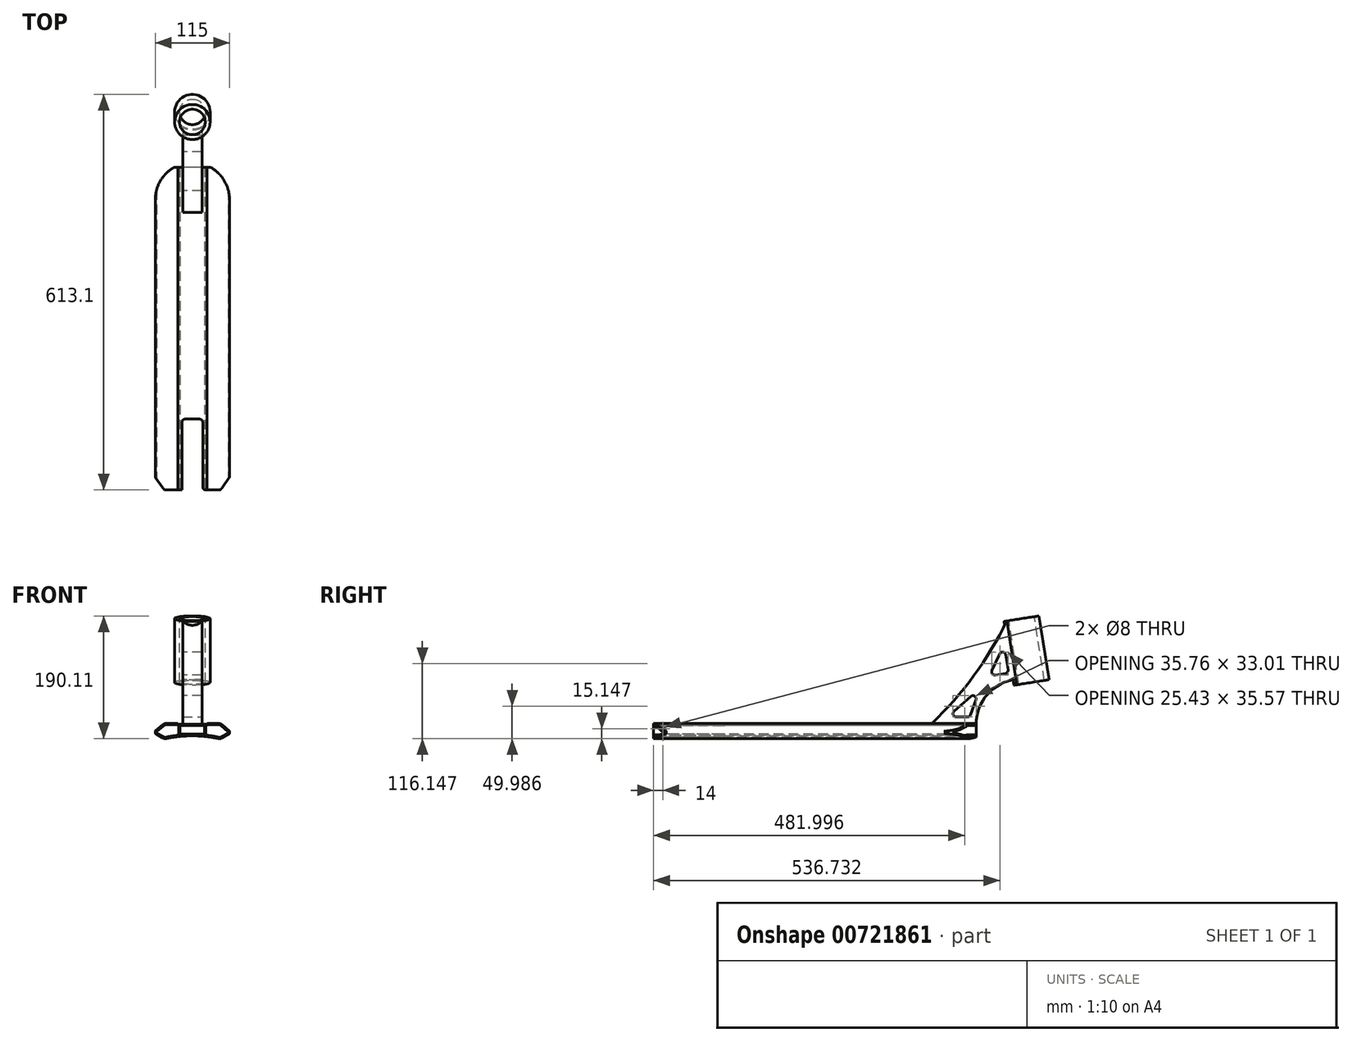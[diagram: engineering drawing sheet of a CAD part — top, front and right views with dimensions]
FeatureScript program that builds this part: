
annotation { "Feature Type Name" : "Feature", "Feature Type Description" : "" }
export const myFeature = defineFeature(function(context is Context, id is Id, definition is map)
    precondition{}
    {
        {
            var Q0;
            Q0=qCreatedBy(makeId("Front.planeOp"),FACE);
            var sketch = newSketch(context, id + "F0", { "sketchPlane" : qUnion([Q0])});
            skLineSegment(sketch, "E0", {"start": v(57.5, 12.15) * mm, "end": v(57.5, 8.15) * mm});
            skLineSegment(sketch, "E1", {"start": v(57.5, 8.15) * mm, "end": v(43.38, 0) * mm});
            skLineSegment(sketch, "E2", {"start": v(0, 0) * mm, "end": v(0, 30.07) * mm, "construction": true});
            skLineSegment(sketch, "E3.MirrorCS", {"start": v(-57.5, 8.15) * mm, "end": v(-43.38, 0) * mm});
            skLineSegment(sketch, "E4.MirrorCS", {"start": v(-57.5, 12.15) * mm, "end": v(-57.5, 8.15) * mm});
            skLineSegment(sketch, "E5", {"start": v(22.5, 24) * mm, "end": v(43.38, 24) * mm});
            skLineSegment(sketch, "E6", {"start": v(43.38, 24) * mm, "end": v(57.5, 12.15) * mm});
            skLineSegment(sketch, "E7.MirrorCS", {"start": v(-22.5, 24) * mm, "end": v(-43.38, 24) * mm});
            skLineSegment(sketch, "E8.MirrorCS", {"start": v(-43.38, 24) * mm, "end": v(-57.5, 12.15) * mm});
            skLineSegment(sketch, "E9", {"start": v(-22.5, 24) * mm, "end": v(-22.5, 22.7) * mm});
            skLineSegment(sketch, "E10", {"start": v(-22.5, 22.7) * mm, "end": v(0, 22.7) * mm});
            skLineSegment(sketch, "E11.MirrorCS", {"start": v(22.5, 24) * mm, "end": v(22.5, 22.7) * mm});
            skLineSegment(sketch, "E12.MirrorCS", {"start": v(22.5, 22.7) * mm, "end": v(0, 22.7) * mm});
            skLineSegment(sketch, "E13", {"start": v(-43.38, 24) * mm, "end": v(-71.32, 24) * mm, "construction": true});
            skLineSegment(sketch, "E14", {"start": v(-57.5, 8.15) * mm, "end": v(-57.5, -4.9) * mm, "construction": true});
            skArc(sketch, "E15", {"start": v(43.38, 0) * mm, "mid": v(0, 4.76) * mm, "end": v(-43.38, 0) * mm});
            skSolve(sketch);
        }
        {
            var Q0;
            Q0=makeQuery(id+"F0.imprint","IMPRINT",FACE,{"disambiguationData":[TD([[makeQuery(id+"F0.imprint","IMPRINT",EDGE,{"derivedFrom":sQuery(id+"F0.wireOp",EDGE,"E0")}),-1.0]])]});
            extrude(context, id + "F1", {"entities" : qUnion([Q0]), "endBound" : BoundingType.SYMMETRIC, "depth" : 500 * mm, "offsetDistance" : 25 * mm});
        }
        {
            var Q0;
            Q0=makeQuery(id+"F1.opExtrude","CAP_FACE",FACE,{"disambiguationData":[OSD([sQuery(id+"F0.wireOp",EDGE,"E0"),sQuery(id+"F0.wireOp",EDGE,"E1"),sQuery(id+"F0.wireOp",EDGE,"E3.MirrorCS"),sQuery(id+"F0.wireOp",EDGE,"E4.MirrorCS"),sQuery(id+"F0.wireOp",EDGE,"E5"),sQuery(id+"F0.wireOp",EDGE,"E6"),sQuery(id+"F0.wireOp",EDGE,"E7.MirrorCS"),sQuery(id+"F0.wireOp",EDGE,"E8.MirrorCS"),sQuery(id+"F0.wireOp",EDGE,"E9"),sQuery(id+"F0.wireOp",EDGE,"E10"),sQuery(id+"F0.wireOp",EDGE,"E11.MirrorCS"),sQuery(id+"F0.wireOp",EDGE,"E12.MirrorCS"),sQuery(id+"F0.wireOp",EDGE,"E15")])],"isStart":false});
            var sketch = newSketch(context, id + "F2", { "sketchPlane" : qUnion([Q0])});
            skLineSegment(sketch, "E16.bottom", {"start": v(19, 7.7) * mm, "end": v(-19, 7.7) * mm});
            skLineSegment(sketch, "E16.top", {"start": v(19, 20.7) * mm, "end": v(-19, 20.7) * mm});
            skLineSegment(sketch, "E16.left", {"start": v(19, 7.7) * mm, "end": v(19, 20.7) * mm});
            skLineSegment(sketch, "E16.right", {"start": v(-19, 7.7) * mm, "end": v(-19, 20.7) * mm});
            skPoint(sketch, "E16.middle", {"position": v(0, 14.2) * mm});
            skSolve(sketch);
        }
        {
            var Q0;
            Q0 = qSketchRegion(id + "F2", true);
            extrude(context, id + "F3", {"entities" : qUnion([Q0]), "operationType" : NewBodyOperationType.REMOVE, "endBound" : BoundingType.SYMMETRIC, "oppositeDirection" : true, "depth" : 1056 * mm, "offsetDistance" : 25 * mm});
        }
        {
            var Q0;
            Q0=makeQuery(id+"F1.opExtrude","SWEPT_EDGE",EDGE,{"disambiguationData":[OSD([sQuery(id+"F0.wireOp",EDGE,"E7.MirrorCS"),sQuery(id+"F0.wireOp",EDGE,"E8.MirrorCS")])]});
            var Q1;
            Q1=makeQuery(id+"F1.opExtrude","SWEPT_EDGE",EDGE,{"disambiguationData":[OSD([sQuery(id+"F0.wireOp",EDGE,"E3.MirrorCS"),sQuery(id+"F0.wireOp",EDGE,"E15")])]});
            var Q2;
            Q2=makeQuery(id+"F1.opExtrude","SWEPT_EDGE",EDGE,{"disambiguationData":[OSD([sQuery(id+"F0.wireOp",EDGE,"E5"),sQuery(id+"F0.wireOp",EDGE,"E6")])]});
            var Q3;
            Q3=makeQuery(id+"F1.opExtrude","SWEPT_EDGE",EDGE,{"disambiguationData":[OSD([sQuery(id+"F0.wireOp",EDGE,"E1"),sQuery(id+"F0.wireOp",EDGE,"E15")])]});
            fillet(context, id + "F4", {"entities" : qUnion([Q0, Q1, Q2, Q3]), "radius" : 9 * mm, "tangentPropagation" : true, "allowEdgeOverflow" : false});
        }
        {
            var Q0;
            Q0=makeQuery(id+"F1.opExtrude","SWEPT_EDGE",EDGE,{"disambiguationData":[OSD([sQuery(id+"F0.wireOp",EDGE,"E4.MirrorCS"),sQuery(id+"F0.wireOp",EDGE,"E8.MirrorCS")])]});
            var Q1;
            Q1=makeQuery(id+"F1.opExtrude","SWEPT_EDGE",EDGE,{"disambiguationData":[OSD([sQuery(id+"F0.wireOp",EDGE,"E3.MirrorCS"),sQuery(id+"F0.wireOp",EDGE,"E4.MirrorCS")])]});
            var Q2;
            Q2=makeQuery(id+"F1.opExtrude","SWEPT_EDGE",EDGE,{"disambiguationData":[OSD([sQuery(id+"F0.wireOp",EDGE,"E0"),sQuery(id+"F0.wireOp",EDGE,"E6")])]});
            var Q3;
            Q3=makeQuery(id+"F1.opExtrude","SWEPT_EDGE",EDGE,{"disambiguationData":[OSD([sQuery(id+"F0.wireOp",EDGE,"E0"),sQuery(id+"F0.wireOp",EDGE,"E1")])]});
            fillet(context, id + "F5", {"entities" : qUnion([Q0, Q1, Q2, Q3]), "radius" : 1 * mm, "tangentPropagation" : true, "allowEdgeOverflow" : false});
        }
        {
            var Q0;
            Q0=makeQuery(id+"F1.opExtrude","SWEPT_EDGE",EDGE,{"disambiguationData":[OSD([sQuery(id+"F0.wireOp",EDGE,"E7.MirrorCS"),sQuery(id+"F0.wireOp",EDGE,"E9")])]});
            var Q1;
            Q1=makeQuery(id+"F1.opExtrude","SWEPT_EDGE",EDGE,{"disambiguationData":[OSD([sQuery(id+"F0.wireOp",EDGE,"E5"),sQuery(id+"F0.wireOp",EDGE,"E11.MirrorCS")])]});
            fillet(context, id + "F6", {"entities" : qUnion([Q0, Q1]), "radius" : 2 * mm, "tangentPropagation" : true, "allowEdgeOverflow" : false});
        }
        {
            var Q0;
            Q0=makeQuery(id+"F1.opExtrude","CAP_FACE",FACE,{"disambiguationData":[OSD([sQuery(id+"F0.wireOp",EDGE,"E0"),sQuery(id+"F0.wireOp",EDGE,"E1"),sQuery(id+"F0.wireOp",EDGE,"E3.MirrorCS"),sQuery(id+"F0.wireOp",EDGE,"E4.MirrorCS"),sQuery(id+"F0.wireOp",EDGE,"E5"),sQuery(id+"F0.wireOp",EDGE,"E6"),sQuery(id+"F0.wireOp",EDGE,"E7.MirrorCS"),sQuery(id+"F0.wireOp",EDGE,"E8.MirrorCS"),sQuery(id+"F0.wireOp",EDGE,"E9"),sQuery(id+"F0.wireOp",EDGE,"E10"),sQuery(id+"F0.wireOp",EDGE,"E11.MirrorCS"),sQuery(id+"F0.wireOp",EDGE,"E12.MirrorCS"),sQuery(id+"F0.wireOp",EDGE,"E15")])],"isStart":false});
            var sketch = newSketch(context, id + "F7", { "sketchPlane" : qUnion([Q0])});
            skArc(sketch, "E17.0", {"start": v(40.47, 2.67) * mm, "mid": v(0, 6.76) * mm, "end": v(-40.47, 2.67) * mm});
            skArc(sketch, "E17.1", {"start": v(-45.38, 3.46) * mm, "mid": v(-43, 2.61) * mm, "end": v(-40.47, 2.67) * mm});
            skLineSegment(sketch, "E17.2", {"start": v(-55, 9.02) * mm, "end": v(-45.38, 3.46) * mm});
            skLineSegment(sketch, "E17.3", {"start": v(-55.5, 10.75) * mm, "end": v(-55.5, 9.88) * mm});
            skLineSegment(sketch, "E17.4", {"start": v(-24.37, 22) * mm, "end": v(-24.37, 22) * mm});
            skLineSegment(sketch, "E17.5", {"start": v(-24.37, 22) * mm, "end": v(-40.1, 22) * mm});
            skArc(sketch, "E17.6", {"start": v(-40.1, 22) * mm, "mid": v(-42.5, 21.58) * mm, "end": v(-44.6, 20.36) * mm});
            skLineSegment(sketch, "E17.7", {"start": v(-44.6, 20.36) * mm, "end": v(-55.14, 11.52) * mm});
            skLineSegment(sketch, "E18.0", {"start": v(-21, 7.7) * mm, "end": v(-21, 20.7) * mm});
            skLineSegment(sketch, "E19.0", {"start": v(19, 20.7) * mm, "end": v(-19, 20.7) * mm});
            skLineSegment(sketch, "E20.0", {"start": v(-22.5, 20.7) * mm, "end": v(22.5, 20.7) * mm});
            skArc(sketch, "E21", {"start": v(-22.5, 20.7) * mm, "mid": v(-23.23, 21.64) * mm, "end": v(-24.37, 22) * mm});
            skLineSegment(sketch, "E22", {"start": v(-21, 7.7) * mm, "end": v(-21, 5.67) * mm});
            skLineSegment(sketch, "E23", {"start": v(0, 0) * mm, "end": v(0, 29.53) * mm});
            skPoint(sketch, "E23.endSnap0", {"position": v(0, 22.7) * mm});
            skLineSegment(sketch, "E24.MirrorCS", {"start": v(21, 7.7) * mm, "end": v(21, 5.67) * mm});
            skLineSegment(sketch, "E25.MirrorCS", {"start": v(21, 7.7) * mm, "end": v(21, 20.7) * mm});
            skLineSegment(sketch, "E26.MirrorCS", {"start": v(22.5, 20.7) * mm, "end": v(-22.5, 20.7) * mm});
            skArc(sketch, "E27.MirrorCS", {"start": v(22.5, 20.7) * mm, "mid": v(23.23, 21.64) * mm, "end": v(24.37, 22) * mm});
            skLineSegment(sketch, "E28.MirrorCS", {"start": v(24.37, 22) * mm, "end": v(40.1, 22) * mm});
            skArc(sketch, "E29.MirrorCS", {"start": v(40.1, 22) * mm, "mid": v(42.5, 21.58) * mm, "end": v(44.6, 20.36) * mm});
            skLineSegment(sketch, "E30.MirrorCS", {"start": v(44.6, 20.36) * mm, "end": v(55.14, 11.52) * mm});
            skLineSegment(sketch, "E31.MirrorCS", {"start": v(55, 9.02) * mm, "end": v(45.38, 3.46) * mm});
            skArc(sketch, "E32.MirrorCS", {"start": v(45.38, 3.46) * mm, "mid": v(43, 2.61) * mm, "end": v(40.47, 2.67) * mm});
            skLineSegment(sketch, "E33.MirrorCS", {"start": v(55.5, 10.75) * mm, "end": v(55.5, 9.88) * mm});
            skPoint(sketch, "E34.visualSharp", {"position": v(-55.5, 11.22) * mm});
            skArc(sketch, "E34.filletArc", {"start": v(-55.14, 11.52) * mm, "mid": v(-55.4, 11.18) * mm, "end": v(-55.5, 10.75) * mm});
            skPoint(sketch, "E35.visualSharp", {"position": v(-55.5, 9.3) * mm});
            skArc(sketch, "E35.filletArc", {"start": v(-55.5, 9.88) * mm, "mid": v(-55.37, 9.38) * mm, "end": v(-55, 9.02) * mm});
            skPoint(sketch, "E36.visualSharp", {"position": v(55.5, 11.22) * mm});
            skArc(sketch, "E36.filletArc", {"start": v(55.5, 10.75) * mm, "mid": v(55.4, 11.18) * mm, "end": v(55.14, 11.52) * mm});
            skPoint(sketch, "E37.visualSharp", {"position": v(55.5, 9.3) * mm});
            skArc(sketch, "E37.filletArc", {"start": v(55, 9.02) * mm, "mid": v(55.37, 9.38) * mm, "end": v(55.5, 9.88) * mm});
            skSolve(sketch);
        }
        {
            var Q0;
            {var subQ3=sQuery(id+"F7.wireOp",EDGE,"E17.1");Q0=makeQuery(id+"F7.imprint","IMPRINT",FACE,{"disambiguationData":[TD([[makeQuery(id+"F7.imprint","IMPRINT",EDGE,{"derivedFrom":subQ3}),1.0]])]});}
            var Q1;
            {var subQ3=sQuery(id+"F7.wireOp",EDGE,"E24.MirrorCS");Q1=makeQuery(id+"F7.imprint","IMPRINT",FACE,{"disambiguationData":[TD([[makeQuery(id+"F7.imprint","IMPRINT",EDGE,{"derivedFrom":subQ3}),1.0]])]});}
            extrude(context, id + "F8", {"entities" : qUnion([Q0, Q1]), "operationType" : NewBodyOperationType.REMOVE, "endBound" : BoundingType.THROUGH_ALL, "oppositeDirection" : true, "depth" : 25 * mm, "offsetDistance" : 25 * mm});
        }
        {
            var Q0;
            Q0=qCreatedBy(makeId("Top.planeOp"),FACE);
            var sketch = newSketch(context, id + "F9", { "sketchPlane" : qUnion([Q0])});
            skArc(sketch, "E38", {"start": v(57.5, 200) * mm, "mid": v(0, 257.5) * mm, "end": v(-57.5, 200) * mm});
            skLineSegment(sketch, "E39", {"start": v(-57.5, 200) * mm, "end": v(-57.5, 280) * mm});
            skLineSegment(sketch, "E40", {"start": v(-57.5, 280) * mm, "end": v(57.5, 280) * mm});
            skLineSegment(sketch, "E41", {"start": v(57.5, 200) * mm, "end": v(57.5, 280) * mm});
            skSolve(sketch);
        }
        {
            var Q0;
            Q0 = qSketchRegion(id + "F9", true);
            extrude(context, id + "F10", {"entities" : qUnion([Q0]), "operationType" : NewBodyOperationType.REMOVE, "endBound" : BoundingType.THROUGH_ALL, "oppositeDirection" : true, "depth" : 25 * mm, "offsetDistance" : 25 * mm, "hasSecondDirection" : true, "secondDirectionBound" : SecondDirectionBoundingType.THROUGH_ALL, "secondDirectionOppositeDirection" : false, "secondDirectionDepth" : 25 * mm});
        }
        {
            var Q0;
            Q0=qCreatedBy(makeId("Top.planeOp"),FACE);
            var sketch = newSketch(context, id + "F11", { "sketchPlane" : qUnion([Q0])});
            skLineSegment(sketch, "E42", {"start": v(-68, -346) * mm, "end": v(-68, -216) * mm});
            skLineSegment(sketch, "E43", {"start": v(-68, -216) * mm, "end": v(-43.3, -250) * mm});
            skLineSegment(sketch, "E44", {"start": v(-43.3, -250) * mm, "end": v(-16, -250) * mm});
            skLineSegment(sketch, "E45", {"start": v(-16, -250) * mm, "end": v(-16, -140) * mm});
            skLineSegment(sketch, "E46", {"start": v(-16, -140) * mm, "end": v(16, -140) * mm});
            skLineSegment(sketch, "E47", {"start": v(16, -140) * mm, "end": v(16, -250) * mm});
            skLineSegment(sketch, "E48", {"start": v(16, -250) * mm, "end": v(43.3, -250) * mm});
            skLineSegment(sketch, "E49", {"start": v(43.3, -250) * mm, "end": v(68, -216) * mm});
            skLineSegment(sketch, "E50", {"start": v(68, -216) * mm, "end": v(68, -346) * mm});
            skLineSegment(sketch, "E51", {"start": v(68, -346) * mm, "end": v(-68, -346) * mm});
            skLineSegment(sketch, "E52", {"start": v(-68, -346) * mm, "end": v(-68, -346) * mm});
            skSolve(sketch);
        }
        {
            var Q0;
            Q0 = qSketchRegion(id + "F11", true);
            extrude(context, id + "F12", {"entities" : qUnion([Q0]), "operationType" : NewBodyOperationType.REMOVE, "endBound" : BoundingType.THROUGH_ALL, "oppositeDirection" : true, "depth" : 25 * mm, "offsetDistance" : 25 * mm, "hasSecondDirection" : true, "secondDirectionBound" : SecondDirectionBoundingType.THROUGH_ALL, "secondDirectionOppositeDirection" : false, "secondDirectionDepth" : 25 * mm});
        }
        {
            var Q0;
            {var subQ0=sQuery(id+"F11.wireOp",EDGE,"E46");var subQ1=sQuery(id+"F11.wireOp",EDGE,"E45");Q0=makeQuery(id+"F12.boolean.opBoolean","COPY",EDGE,{"disambiguationData":[TD([makeQuery(id+"F3.boolean.opBoolean","COPY",FACE,{"derivedFrom":makeQuery(id+"F3.opExtrude","SWEPT_FACE",FACE,{"disambiguationData":[OSD([sQuery(id+"F2.wireOp",EDGE,"E16.top")])]})})])],"derivedFrom":makeQuery(id+"F12.opExtrude","SWEPT_EDGE",EDGE,{"disambiguationData":[OSD([subQ1,subQ0])]})});}
            var Q1;
            {var subQ0=sQuery(id+"F11.wireOp",EDGE,"E45");var subQ1=sQuery(id+"F11.wireOp",EDGE,"E46");Q1=makeQuery(id+"F12.boolean.opBoolean","COPY",EDGE,{"disambiguationData":[TD([makeQuery(id+"F1.opExtrude","SWEPT_FACE",FACE,{"disambiguationData":[OSD([sQuery(id+"F0.wireOp",EDGE,"E15")])]})])],"derivedFrom":makeQuery(id+"F12.opExtrude","SWEPT_EDGE",EDGE,{"disambiguationData":[OSD([subQ0,subQ1])]})});}
            var Q2;
            {var subQ0=sQuery(id+"F11.wireOp",EDGE,"E46");var subQ1=sQuery(id+"F11.wireOp",EDGE,"E47");Q2=makeQuery(id+"F12.boolean.opBoolean","COPY",EDGE,{"disambiguationData":[TD([makeQuery(id+"F3.boolean.opBoolean","COPY",FACE,{"derivedFrom":makeQuery(id+"F3.opExtrude","SWEPT_FACE",FACE,{"disambiguationData":[OSD([sQuery(id+"F2.wireOp",EDGE,"E16.top")])]})})])],"derivedFrom":makeQuery(id+"F12.opExtrude","SWEPT_EDGE",EDGE,{"disambiguationData":[OSD([subQ0,subQ1])]})});}
            var Q3;
            {var subQ0=sQuery(id+"F11.wireOp",EDGE,"E46");var subQ1=sQuery(id+"F11.wireOp",EDGE,"E47");Q3=makeQuery(id+"F12.boolean.opBoolean","COPY",EDGE,{"disambiguationData":[TD([makeQuery(id+"F1.opExtrude","SWEPT_FACE",FACE,{"disambiguationData":[OSD([sQuery(id+"F0.wireOp",EDGE,"E15")])]})])],"derivedFrom":makeQuery(id+"F12.opExtrude","SWEPT_EDGE",EDGE,{"disambiguationData":[OSD([subQ0,subQ1])]})});}
            var Q4;
            {var subQ2=sQuery(id+"F11.wireOp",EDGE,"E45");Q4=makeQuery(id+"F12.boolean.opBoolean","COPY",EDGE,{"disambiguationData":[TD([makeQuery(id+"F3.boolean.opBoolean","COPY",FACE,{"derivedFrom":makeQuery(id+"F3.opExtrude","SWEPT_FACE",FACE,{"disambiguationData":[OSD([sQuery(id+"F2.wireOp",EDGE,"E16.top")])]})})])],"derivedFrom":makeQuery(id+"F12.opExtrude","SWEPT_EDGE",EDGE,{"disambiguationData":[OSD([sQuery(id+"F11.wireOp",EDGE,"E44"),subQ2])]})});}
            var Q5;
            {var subQ0=sQuery(id+"F0.wireOp",EDGE,"E15");var subQ1=sQuery(id+"F11.wireOp",EDGE,"E47");Q5=makeQuery(id+"F12.boolean.opBoolean","COPY",EDGE,{"disambiguationData":[TD([makeQuery(id+"F1.opExtrude","SWEPT_FACE",FACE,{"disambiguationData":[OSD([subQ0])]})])],"derivedFrom":makeQuery(id+"F12.opExtrude","SWEPT_EDGE",EDGE,{"disambiguationData":[OSD([subQ1,sQuery(id+"F11.wireOp",EDGE,"E48")])]})});}
            fillet(context, id + "F13", {"entities" : qUnion([Q0, Q1, Q2, Q3, Q4, Q5]), "radius" : 5 * mm, "tangentPropagation" : true, "allowEdgeOverflow" : false});
        }
        {
            var Q0;
            Q0=qCreatedBy(makeId("Right.planeOp"),FACE);
            var sketch = newSketch(context, id + "F14", { "sketchPlane" : qUnion([Q0])});
            skLineSegment(sketch, "E53", {"start": v(180, 22.7) * mm, "end": v(250, 22.7) * mm});
            skArc(sketch, "E54", {"start": v(180, 22.7) * mm, "mid": v(245.97, 97.36) * mm, "end": v(297.38, 182.7) * mm});
            skLineSegment(sketch, "E55", {"start": v(297.38, 182.7) * mm, "end": v(342.82, 189.9) * mm});
            skLineSegment(sketch, "E56", {"start": v(342.82, 189.9) * mm, "end": v(358.46, 91.13) * mm});
            skLineSegment(sketch, "E57", {"start": v(358.46, 91.13) * mm, "end": v(313.03, 83.93) * mm});
            skLineSegment(sketch, "E58", {"start": v(313.03, 83.93) * mm, "end": v(311.71, 92.2) * mm});
            skArc(sketch, "E59", {"start": v(311.71, 92.2) * mm, "mid": v(267.66, 69.18) * mm, "end": v(250, 22.7) * mm});
            skSolve(sketch);
        }
        {
            var Q0;
            Q0=makeQuery(id+"F14.imprint","IMPRINT",FACE,{"disambiguationData":[TD([[makeQuery(id+"F14.imprint","IMPRINT",EDGE,{"derivedFrom":sQuery(id+"F14.wireOp",EDGE,"E53")}),1.0]])]});
            extrude(context, id + "F15", {"entities" : qUnion([Q0]), "operationType" : NewBodyOperationType.ADD, "endBound" : BoundingType.SYMMETRIC, "depth" : 30 * mm, "offsetDistance" : 25 * mm});
        }
        {
            var Q0;
            Q0=makeQuery(id+"F15.opExtrude","SWEPT_FACE",FACE,{"disambiguationData":[OSD([sQuery(id+"F14.wireOp",EDGE,"E55")])]});
            var sketch = newSketch(context, id + "F16", { "sketchPlane" : qUnion([Q0])});
            skCircle(sketch, "E60", {"center": v(0, 345.5) * mm, "radius": 27.5 * mm});
            skSolve(sketch);
        }
        {
            var Q0;
            Q0 = qSketchRegion(id + "F16", true);
            var Q1;
            Q1=makeQuery(id+"F15.opExtrude","SWEPT_FACE",FACE,{"disambiguationData":[OSD([sQuery(id+"F14.wireOp",EDGE,"E57")])]});
            extrude(context, id + "F17", {"entities" : qUnion([Q0]), "operationType" : NewBodyOperationType.ADD, "endBound" : BoundingType.UP_TO_SURFACE, "oppositeDirection" : true, "depth" : 25 * mm, "endBoundEntityFace" : qUnion([Q1]), "offsetDistance" : 25 * mm});
        }
        {
            var Q0;
            Q0=makeQuery(id+"F17.boolean.opBoolean","MERGE",FACE,{"derivedFrom":[makeQuery(id+"F15.opExtrude","SWEPT_FACE",FACE,{"disambiguationData":[OSD([sQuery(id+"F14.wireOp",EDGE,"E55")])]}),makeQuery(id+"F17.opExtrude","CAP_FACE",FACE,{"disambiguationData":[OSD([sQuery(id+"F16.wireOp",EDGE,"E60")])],"isStart":true})]});
            var sketch = newSketch(context, id + "F18", { "sketchPlane" : qUnion([Q0])});
            skPoint(sketch, "E61", {"position": v(0, 345.5) * mm});
            skSolve(sketch);
        }
        {
            var Q0;
            Q0=makeQuery(id+"F8.boolean.opBoolean","COPY",FACE,{"derivedFrom":makeQuery(id+"F8.opExtrude","SWEPT_FACE",FACE,{"disambiguationData":[OSD([sQuery(id+"F7.wireOp",EDGE,"E24.MirrorCS"),sQuery(id+"F7.wireOp",EDGE,"E25.MirrorCS")])]})});
            var sketch = newSketch(context, id + "F19", { "sketchPlane" : qUnion([Q0])});
            skPoint(sketch, "E62", {"position": v(-236, 15.67) * mm});
            skSolve(sketch);
        }
        {
            var Q0;
            Q0=sQuery(id+"F18.wireOp",VERTEX,"E61");
            var Q1;
            Q1=makeQuery(id+"F1.opExtrude","SWEPT_BODY",BODY,{"disambiguationData":[OSD([sQuery(id+"F0.wireOp",EDGE,"E0"),sQuery(id+"F0.wireOp",EDGE,"E1"),sQuery(id+"F0.wireOp",EDGE,"E3.MirrorCS"),sQuery(id+"F0.wireOp",EDGE,"E4.MirrorCS"),sQuery(id+"F0.wireOp",EDGE,"E5"),sQuery(id+"F0.wireOp",EDGE,"E6"),sQuery(id+"F0.wireOp",EDGE,"E7.MirrorCS"),sQuery(id+"F0.wireOp",EDGE,"E8.MirrorCS"),sQuery(id+"F0.wireOp",EDGE,"E9"),sQuery(id+"F0.wireOp",EDGE,"E10"),sQuery(id+"F0.wireOp",EDGE,"E11.MirrorCS"),sQuery(id+"F0.wireOp",EDGE,"E12.MirrorCS"),sQuery(id+"F0.wireOp",EDGE,"E15")])]});
            hole(context, id + "F20", {"style" : HoleStyle.SIMPLE, "endStyle" : HoleEndStyle.THROUGH, "holeDiameter" : 40 * mm, "majorDiameter" : 5 * mm, "isTappedThrough" : true, "tappedDepth" : 12 * mm, "tapClearance" : 3, "locations" : qUnion([Q0]), "scope" : qUnion([Q1])});
        }
        {
            var Q0;
            Q0=sQuery(id+"F19.wireOp",VERTEX,"E62");
            var Q1;
            Q1=makeQuery(id+"F1.opExtrude","SWEPT_BODY",BODY,{"disambiguationData":[OSD([sQuery(id+"F0.wireOp",EDGE,"E0"),sQuery(id+"F0.wireOp",EDGE,"E1"),sQuery(id+"F0.wireOp",EDGE,"E3.MirrorCS"),sQuery(id+"F0.wireOp",EDGE,"E4.MirrorCS"),sQuery(id+"F0.wireOp",EDGE,"E5"),sQuery(id+"F0.wireOp",EDGE,"E6"),sQuery(id+"F0.wireOp",EDGE,"E7.MirrorCS"),sQuery(id+"F0.wireOp",EDGE,"E8.MirrorCS"),sQuery(id+"F0.wireOp",EDGE,"E9"),sQuery(id+"F0.wireOp",EDGE,"E10"),sQuery(id+"F0.wireOp",EDGE,"E11.MirrorCS"),sQuery(id+"F0.wireOp",EDGE,"E12.MirrorCS"),sQuery(id+"F0.wireOp",EDGE,"E15")])]});
            hole(context, id + "F21", {"style" : HoleStyle.SIMPLE, "endStyle" : HoleEndStyle.BLIND, "holeDiameter" : 8 * mm, "majorDiameter" : 5 * mm, "holeDepth" : 50 * mm, "isTappedThrough" : true, "tappedDepth" : 12 * mm, "tapClearance" : 3, "locations" : qUnion([Q0]), "scope" : qUnion([Q1])});
        }
        {
            var Q0;
            Q0=makeQuery(id+"F15.opExtrude","CAP_FACE",FACE,{"disambiguationData":[OSD([sQuery(id+"F14.wireOp",EDGE,"E53"),sQuery(id+"F14.wireOp",EDGE,"E54"),sQuery(id+"F14.wireOp",EDGE,"E55"),sQuery(id+"F14.wireOp",EDGE,"E56"),sQuery(id+"F14.wireOp",EDGE,"E57"),sQuery(id+"F14.wireOp",EDGE,"E58"),sQuery(id+"F14.wireOp",EDGE,"E59")])],"isStart":false});
            var sketch = newSketch(context, id + "F22", { "sketchPlane" : qUnion([Q0])});
            skLineSegment(sketch, "E63", {"start": v(206, 34) * mm, "end": v(240, 34) * mm});
            skLineSegment(sketch, "E64", {"start": v(240, 34) * mm, "end": v(256.38, 79) * mm});
            skLineSegment(sketch, "E65", {"start": v(256.38, 79) * mm, "end": v(206, 34) * mm});
            skLineSegment(sketch, "E66", {"start": v(270.54, 97.45) * mm, "end": v(293.13, 146.6) * mm});
            skLineSegment(sketch, "E67", {"start": v(293.13, 146.6) * mm, "end": v(300.17, 102.14) * mm});
            skLineSegment(sketch, "E68", {"start": v(300.17, 102.14) * mm, "end": v(270.54, 97.45) * mm});
            skSolve(sketch);
        }
        {
            var Q0;
            Q0 = qSketchRegion(id + "F22", true);
            extrude(context, id + "F23", {"entities" : qUnion([Q0]), "operationType" : NewBodyOperationType.REMOVE, "endBound" : BoundingType.THROUGH_ALL, "oppositeDirection" : true, "depth" : 25 * mm, "offsetDistance" : 25 * mm});
        }
        {
            var Q0;
            Q0=makeQuery(id+"F23.boolean.opBoolean","COPY",EDGE,{"derivedFrom":makeQuery(id+"F23.opExtrude","SWEPT_EDGE",EDGE,{"disambiguationData":[OSD([sQuery(id+"F22.wireOp",EDGE,"E67"),sQuery(id+"F22.wireOp",EDGE,"E68")])]})});
            var Q1;
            Q1=makeQuery(id+"F23.boolean.opBoolean","COPY",EDGE,{"derivedFrom":makeQuery(id+"F23.opExtrude","SWEPT_EDGE",EDGE,{"disambiguationData":[OSD([sQuery(id+"F22.wireOp",EDGE,"E66"),sQuery(id+"F22.wireOp",EDGE,"E68")])]})});
            var Q2;
            Q2=makeQuery(id+"F23.boolean.opBoolean","COPY",EDGE,{"derivedFrom":makeQuery(id+"F23.opExtrude","SWEPT_EDGE",EDGE,{"disambiguationData":[OSD([sQuery(id+"F22.wireOp",EDGE,"E66"),sQuery(id+"F22.wireOp",EDGE,"E67")])]})});
            var Q3;
            Q3=makeQuery(id+"F23.boolean.opBoolean","COPY",EDGE,{"derivedFrom":makeQuery(id+"F23.opExtrude","SWEPT_EDGE",EDGE,{"disambiguationData":[OSD([sQuery(id+"F22.wireOp",EDGE,"E64"),sQuery(id+"F22.wireOp",EDGE,"E65")])]})});
            var Q4;
            Q4=makeQuery(id+"F23.boolean.opBoolean","COPY",EDGE,{"derivedFrom":makeQuery(id+"F23.opExtrude","SWEPT_EDGE",EDGE,{"disambiguationData":[OSD([sQuery(id+"F22.wireOp",EDGE,"E63"),sQuery(id+"F22.wireOp",EDGE,"E64")])]})});
            var Q5;
            Q5=makeQuery(id+"F23.boolean.opBoolean","COPY",EDGE,{"derivedFrom":makeQuery(id+"F23.opExtrude","SWEPT_EDGE",EDGE,{"disambiguationData":[OSD([sQuery(id+"F22.wireOp",EDGE,"E63"),sQuery(id+"F22.wireOp",EDGE,"E65")])]})});
            fillet(context, id + "F24", {"entities" : qUnion([Q0, Q1, Q2, Q3, Q4, Q5]), "radius" : 5 * mm, "tangentPropagation" : true, "allowEdgeOverflow" : false});
        }
    });
